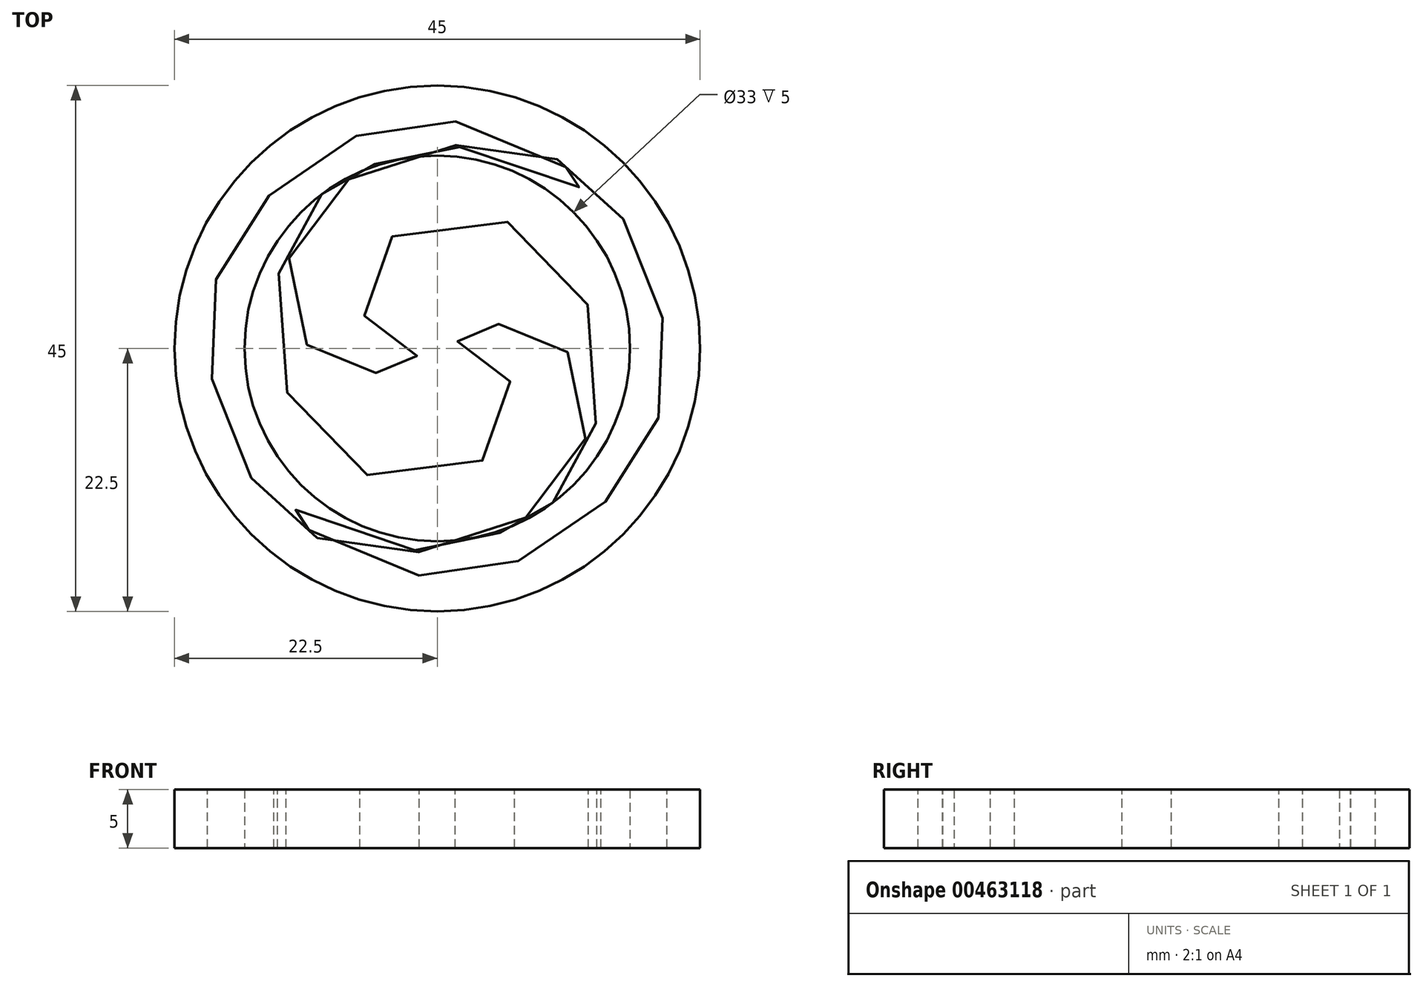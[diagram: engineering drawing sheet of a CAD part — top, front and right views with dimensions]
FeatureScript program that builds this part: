
annotation { "Feature Type Name" : "Feature", "Feature Type Description" : "" }
export const myFeature = defineFeature(function(context is Context, id is Id, definition is map)
    precondition{}
    {
        {
            var Q0;
            Q0=qCreatedBy(makeId("Top.planeOp"),FACE);
            var sketch = newSketch(context, id + "F0", { "sketchPlane" : qUnion([Q0])});
            skCircle(sketch, "E0", {"center": v(0, 0) * mm, "radius": 22.5 * mm});
            skCircle(sketch, "E1", {"center": v(0, 0) * mm, "radius": 16.5 * mm});
            skSolve(sketch);
        }
        {
            var Q0;
            Q0 = qSketchRegion(id + "F0", true);
            extrude(context, id + "F1", {"entities" : qUnion([Q0]), "depth" : 5 * mm});
        }
        {
            var Q0;
            Q0=makeQuery(id+"F1.opExtrude","CAP_FACE",FACE,{"disambiguationData":[OSD([sQuery(id+"F0.wireOp",EDGE,"E0"),sQuery(id+"F0.wireOp",EDGE,"E1")])],"isStart":false});
            var sketch = newSketch(context, id + "F2", { "sketchPlane" : qUnion([Q0])});
            skFitSpline(sketch, "E2", {"points": [v(-9.88, 13.21) * mm, v(-13.97, 3.68) * mm, v(-7.46, -10.27) * mm, v(5.76, -7.83) * mm, v(4.75, -0.71) * mm, v(1.56, 0.78) * mm, v(3.53, 1.8) * mm, v(9.66, 1.1) * mm, v(12.88, -6.54) * mm, v(6.12, -15.32) * mm, v(-7.74, -17.03) * mm, v(-15.28, -12.02) * mm, v(-19.63, 0) * mm, v(-16.7, 10.38) * mm, v(-6.84, 18.23) * mm, v(5.44, 18.4) * mm, v(13.63, 13.38) * mm, v(0.95, 17.39) * mm, v(-6.28, 15.26) * mm, v(-9.88, 13.21) * mm]});
            skCircle(sketch, "E3", {"center": v(0, 0) * mm, "radius": 9.72 * mm, "construction": true});
            skCircle(sketch, "E4", {"center": v(0, 0) * mm, "radius": 14.45 * mm, "construction": true});
            skSolve(sketch);
        }
        {
            var Q0;
            Q0 = qSketchRegion(id + "F2", true);
            var Q1;
            Q1=makeQuery(id+"F1.opExtrude","CAP_FACE",FACE,{"disambiguationData":[OSD([sQuery(id+"F0.wireOp",EDGE,"E0"),sQuery(id+"F0.wireOp",EDGE,"E1")])],"isStart":true});
            extrude(context, id + "F3", {"entities" : qUnion([Q0]), "endBound" : BoundingType.UP_TO_SURFACE, "oppositeDirection" : true, "endBoundEntityFace" : qUnion([Q1]), "depth" : 25 * mm});
        }
        {
            var Q0;
            Q0=qCreatedBy(makeId("Right.planeOp"),FACE);
            var sketch = newSketch(context, id + "F4", { "sketchPlane" : qUnion([Q0])});
            skLineSegment(sketch, "E5", {"start": v(0, 52.15) * mm, "end": v(0, -55.7) * mm, "construction": true});
            skSolve(sketch);
        }
        {
            var Q0;
            Q0=makeQuery(id+"F3.opExtrude","SWEPT_BODY",BODY,{"disambiguationData":[OSD([sQuery(id+"F2.wireOp",EDGE,"E2")])]});
            var Q1;
            Q1=sQuery(id+"F4.wireOp",EDGE,"E5");
            circularPattern(context, id + "F5", {"entities" : qUnion([Q0]), "axis" : qUnion([Q1]), "angle" : 360 * degree, "instanceCount" : 2, "equalSpace" : true});
        }
    });
